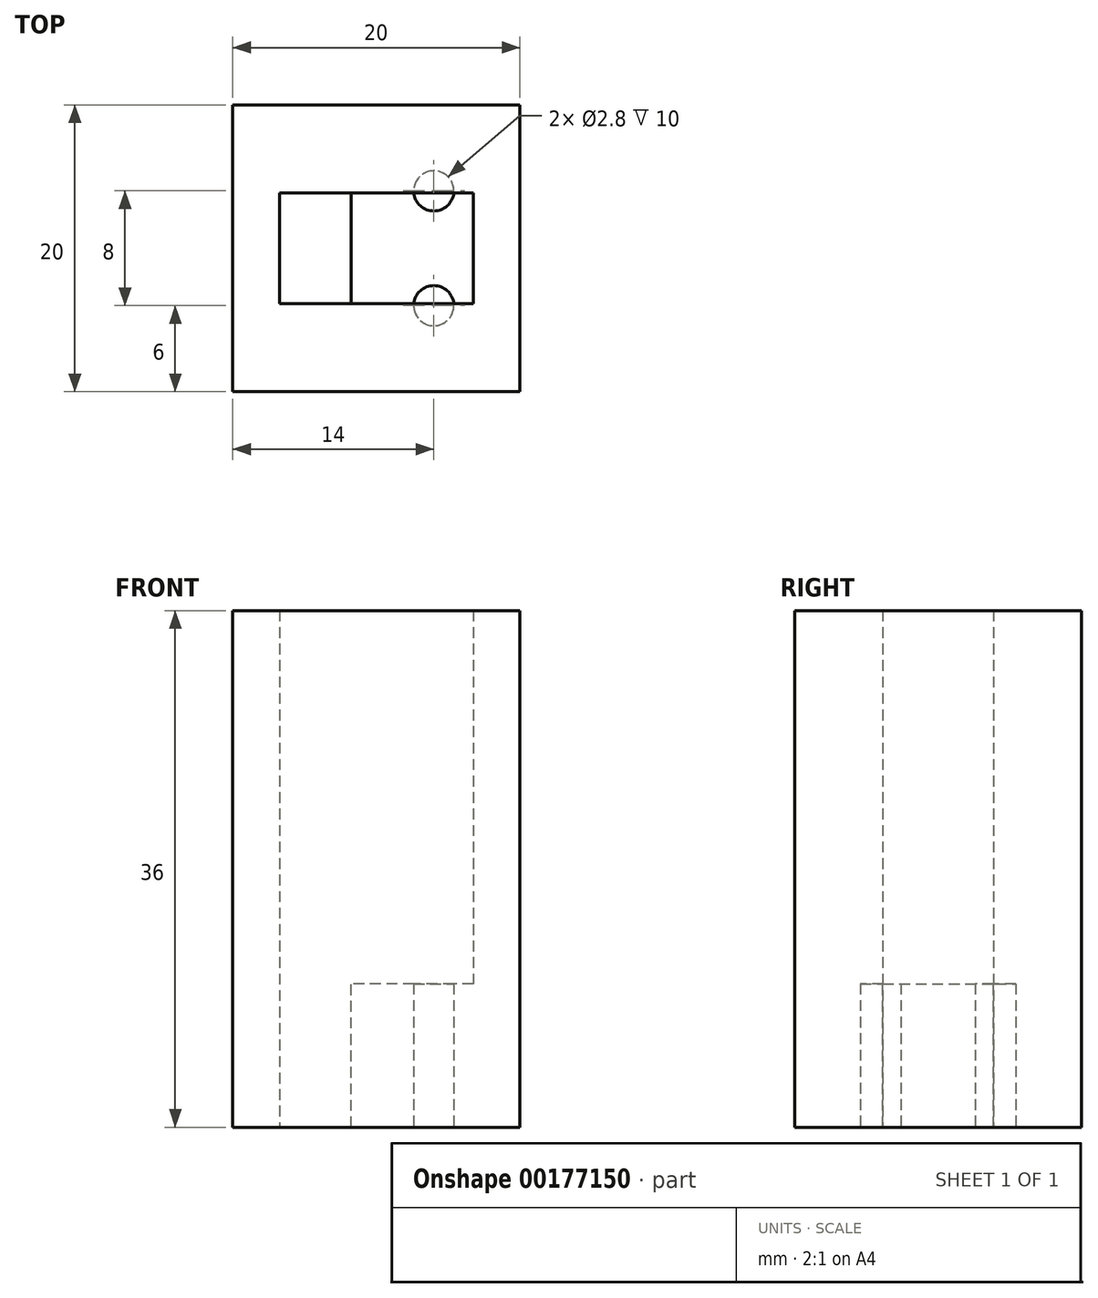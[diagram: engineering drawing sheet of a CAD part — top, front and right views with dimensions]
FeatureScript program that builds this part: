
annotation { "Feature Type Name" : "Feature", "Feature Type Description" : "" }
export const myFeature = defineFeature(function(context is Context, id is Id, definition is map)
    precondition{}
    {
        {
            var Q0;
            Q0=qCreatedBy(makeId("Top.planeOp"),FACE);
            var sketch = newSketch(context, id + "F0", { "sketchPlane" : qUnion([Q0])});
            skLineSegment(sketch, "E0.bottom", {"start": v(10, -10) * mm, "end": v(-10, -10) * mm});
            skLineSegment(sketch, "E0.top", {"start": v(10, 10) * mm, "end": v(-10, 10) * mm});
            skLineSegment(sketch, "E0.left", {"start": v(10, -10) * mm, "end": v(10, 10) * mm});
            skLineSegment(sketch, "E0.right", {"start": v(-10, -10) * mm, "end": v(-10, 10) * mm});
            skPoint(sketch, "E0.middle", {"position": v(0, 0) * mm});
            skLineSegment(sketch, "E1.bottom", {"start": v(6.75, -3.85) * mm, "end": v(-6.75, -3.85) * mm});
            skLineSegment(sketch, "E1.top", {"start": v(6.75, 3.85) * mm, "end": v(-6.75, 3.85) * mm});
            skLineSegment(sketch, "E1.left", {"start": v(6.75, -3.85) * mm, "end": v(6.75, 3.85) * mm});
            skLineSegment(sketch, "E1.right", {"start": v(-6.75, -3.85) * mm, "end": v(-6.75, 3.85) * mm});
            skSolve(sketch);
        }
        {
            var Q0;
            Q0=qSketchRegion(id+"F0",true);
            extrude(context, id + "F1", {"entities" : qUnion([Q0]), "depth" : 26 * mm});
        }
        {
            var Q0;
            Q0=qCreatedBy(makeId("Top.planeOp"),FACE);
            var sketch = newSketch(context, id + "F2", { "sketchPlane" : qUnion([Q0])});
            skLineSegment(sketch, "E2.bottom", {"start": v(-6.75, 3.85) * mm, "end": v(-1.75, 3.85) * mm});
            skLineSegment(sketch, "E2.top", {"start": v(-6.75, -3.85) * mm, "end": v(-1.75, -3.85) * mm});
            skLineSegment(sketch, "E2.left", {"start": v(-6.75, 3.85) * mm, "end": v(-6.75, -3.85) * mm});
            skLineSegment(sketch, "E2.right", {"start": v(-1.75, 3.85) * mm, "end": v(-1.75, -3.85) * mm});
            skLineSegment(sketch, "E3.bottom", {"start": v(10, 10) * mm, "end": v(-10, 10) * mm});
            skLineSegment(sketch, "E3.top", {"start": v(10, -10) * mm, "end": v(-10, -10) * mm});
            skLineSegment(sketch, "E3.left", {"start": v(10, 10) * mm, "end": v(10, -10) * mm});
            skLineSegment(sketch, "E3.right", {"start": v(-10, 10) * mm, "end": v(-10, -10) * mm});
            skPoint(sketch, "E3.middle", {"position": v(0, 0) * mm});
            skSolve(sketch);
        }
        {
            var Q0;
            Q0=qSketchRegion(id+"F2",true);
            extrude(context, id + "F3", {"entities" : qUnion([Q0]), "operationType" : NewBodyOperationType.ADD, "oppositeDirection" : true, "depth" : 10 * mm});
        }
        {
            var Q0;
            Q0=makeQuery(id+"F3.opExtrude","CAP_FACE",FACE,{"disambiguationData":[OSD([sQuery(id+"F2.wireOp",EDGE,"E2.bottom"),sQuery(id+"F2.wireOp",EDGE,"E2.top"),sQuery(id+"F2.wireOp",EDGE,"E2.left"),sQuery(id+"F2.wireOp",EDGE,"E2.right"),sQuery(id+"F2.wireOp",EDGE,"E3.bottom"),sQuery(id+"F2.wireOp",EDGE,"E3.top"),sQuery(id+"F2.wireOp",EDGE,"E3.left"),sQuery(id+"F2.wireOp",EDGE,"E3.right")])],"isStart":false});
            var sketch = newSketch(context, id + "F4", { "sketchPlane" : qUnion([Q0])});
            skCircle(sketch, "E4", {"center": v(4, 4) * mm, "radius": 1.4 * mm});
            skCircle(sketch, "E5", {"center": v(4, -4) * mm, "radius": 1.4 * mm});
            skSolve(sketch);
        }
        {
            var Q0;
            Q0=qSketchRegion(id+"F4",true);
            extrude(context, id + "F5", {"entities" : qUnion([Q0]), "operationType" : NewBodyOperationType.REMOVE, "oppositeDirection" : true, "depth" : 10 * mm});
        }
    });
